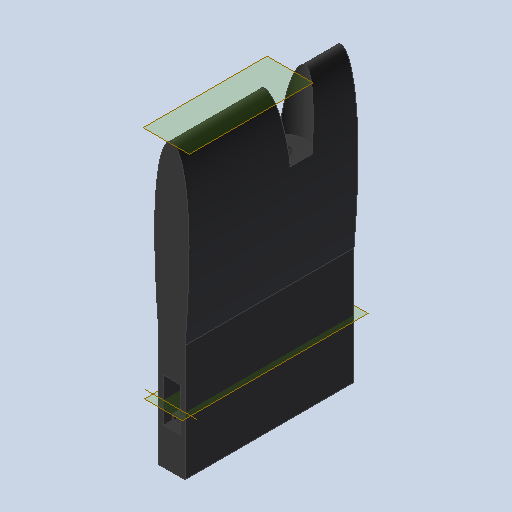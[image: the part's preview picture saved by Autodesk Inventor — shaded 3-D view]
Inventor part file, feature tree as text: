
AUTODESK INVENTOR PART (.ipt)
format: ipt  version: 2025.2 (Build 292293000, 293)  size: 183,296 bytes
history: native  units: in
note: dims shown in document units (in); Inventor stores cm internally (conversion verified against a paired STEP export)
features: other x7, plane x4, sketch x1
ambient origin geometry x8: Origin, YZ Plane, XZ Plane, XY Plane, X Axis, Y Axis, Z Axis, Center Point
bodies: Solid1 (feature_tree)
feature tree (12):
  other  "OuterTailLeft.ipt"
  other  "Solid1::OuterTailLeft.ipt"
  other  "TaggingFeature1"
  sketch  "Sketch1"  dims[d0=0.3937in]
  plane  "Work Plane1"
  plane  "Work Plane4"
  plane  "Work Plane5"
  plane  "Work Plane6"
  other  "Work Axis1"
  other  "Work Axis2"
  other  "Work Axis3"
  other  "Work Point1"
